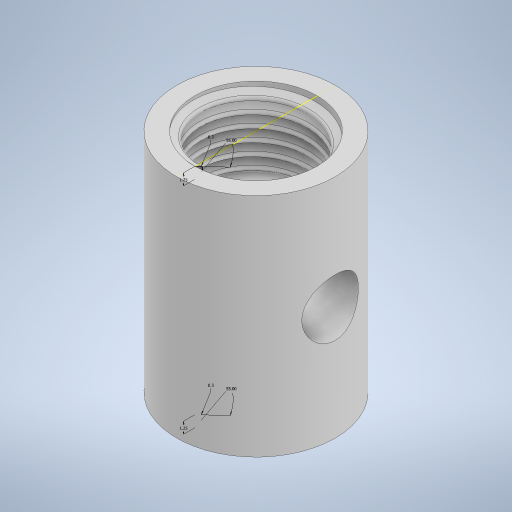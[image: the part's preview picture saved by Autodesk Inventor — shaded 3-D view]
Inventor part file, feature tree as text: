
AUTODESK INVENTOR PART (.ipt)
format: ipt  version: 2023 (Build 270158000, 158)  size: 629,760 bytes
history: native  units: mm
features: sketch x8, extrude x4, revolve x2, helix x2, projected_geometry x2, fillet x1, plane x1, mirror x1
ambient origin geometry x8: Origin, YZ Plane, XZ Plane, XY Plane, X Axis, Y Axis, Z Axis, Center Point
bodies: Solid1 (feature_tree)
feature tree (21):
  extrude  "Extrusion1"  Depth=6.0mm
  revolve  "Revolution1"  [1 undecoded]
  sketch  "Sketch3"  dims[d6=90.0deg d7=9.599311mm]
  helix  "Coil1"  [1 undecoded]
  extrude  "Extrusion2"  Depth=9.599311mm
  extrude  "Extrusion3"  Depth=0.3mm
  fillet  "Fillet1"  Radius=20.0mm
  sketch  "Sketch6"  dims[d30=0.55mm d31=0.0mm d32=0.2mm]
  helix  "Coil3"  [1 undecoded]
  extrude  "Extrusion4"  Depth=0.2mm
  plane  "Work Plane2"
  mirror  "Mirror2"
  revolve  "Revolution2"  [1 undecoded]
  sketch  "Sketch1"  dims[d0=17.5mm d1=6.0mm]
  sketch  "Sketch2"  dims[d2=25.0mm d3=0.0mm d4=6.75mm d5=8.05mm]
  projected_geometry  "Projected Loop1"
  sketch  "Sketch4"  dims[d8=1.25mm d9=0.3mm]
  projected_geometry  "Projected Loop2"
  sketch  "Sketch5"  dims[d10=1.337mm d11=9.2mm d12=90.0mm d13=0.0mm d14=90.0deg d15=90.0deg d16=0.0mm d17=0.0mm d27=20.0mm d28=0.0mm d29=7.5mm]
  sketch  "Sketch7"  dims[d33=9.599311mm d34=1.25mm d35=0.3mm]
  sketch  "Sketch10"  dims[d42=1.337mm d43=9.2mm d44=90.0mm d45=0.0mm d46=90.0deg d47=90.0deg d48=0.0mm d49=0.0mm d58=0.0mm d59=0.0mm d60=5.9mm d61=6.3mm d62=360.0deg d63=4.0mm]
note: 4 required parameter values undecoded (feature->parameter linkage not recoverable at this tier; creation-order binding heuristic only, values carry confidence <= 0.55)